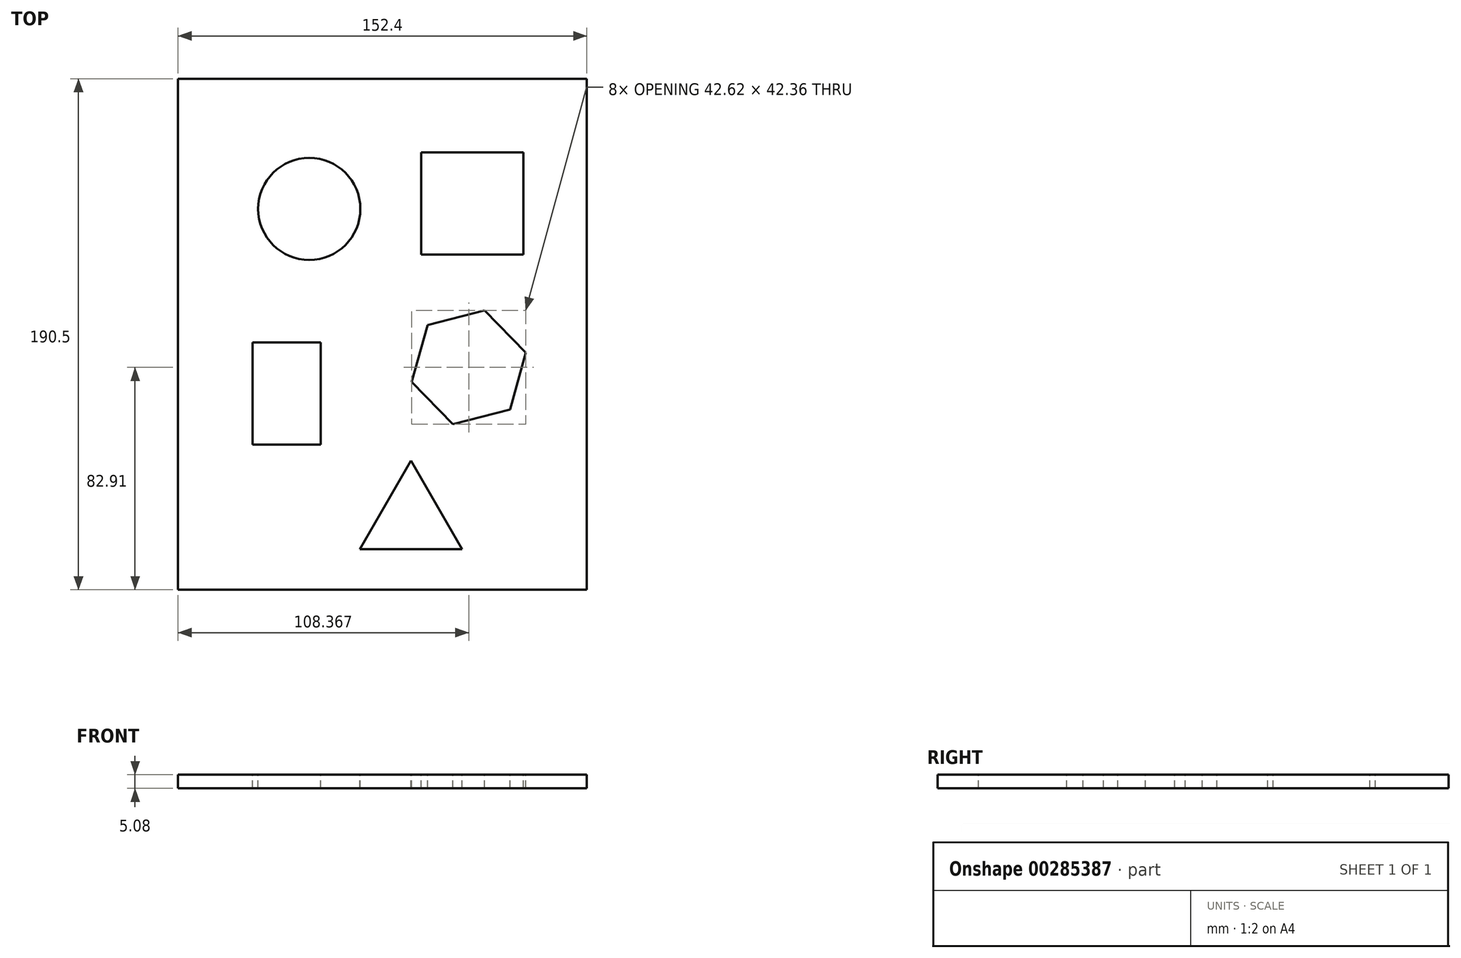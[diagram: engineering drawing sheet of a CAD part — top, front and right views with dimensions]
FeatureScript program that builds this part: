
annotation { "Feature Type Name" : "Feature", "Feature Type Description" : "" }
export const myFeature = defineFeature(function(context is Context, id is Id, definition is map)
    precondition{}
    {
        {
            var Q0;
            Q0=qCreatedBy(makeId("Top.planeOp"),FACE);
            var sketch = newSketch(context, id + "F0", { "sketchPlane" : qUnion([Q0])});
            skLineSegment(sketch, "E0.bottom", {"start": v(-86.56, 107.59) * mm, "end": v(65.84, 107.59) * mm});
            skLineSegment(sketch, "E0.top", {"start": v(-86.56, -82.91) * mm, "end": v(65.84, -82.91) * mm});
            skLineSegment(sketch, "E0.left", {"start": v(-86.56, 107.59) * mm, "end": v(-86.56, -82.91) * mm});
            skLineSegment(sketch, "E0.right", {"start": v(65.84, 107.59) * mm, "end": v(65.84, -82.91) * mm});
            skSolve(sketch);
        }
        {
            var Q0;
            Q0=makeQuery(id+"F0.imprint","IMPRINT",FACE,{"disambiguationData":[TD([[makeQuery(id+"F0.imprint","IMPRINT",EDGE,{"derivedFrom":sQuery(id+"F0.wireOp",EDGE,"E0.bottom")}),-1.0]])]});
            extrude(context, id + "F1", {"entities" : qUnion([Q0]), "depth" : 5.08 * mm});
        }
        {
            var Q0;
            Q0=makeQuery(id+"F1.opExtrude","CAP_FACE",FACE,{"disambiguationData":[OSD([sQuery(id+"F0.wireOp",EDGE,"E0.bottom"),sQuery(id+"F0.wireOp",EDGE,"E0.top"),sQuery(id+"F0.wireOp",EDGE,"E0.left"),sQuery(id+"F0.wireOp",EDGE,"E0.right")])],"isStart":false});
            var sketch = newSketch(context, id + "F2", { "sketchPlane" : qUnion([Q0])});
            skCircle(sketch, "E1", {"center": v(-37.64, 59.09) * mm, "radius": 19.05 * mm});
            skLineSegment(sketch, "E2.bottom", {"start": v(4.04, 80.2) * mm, "end": v(42.14, 80.2) * mm});
            skLineSegment(sketch, "E2.top", {"start": v(4.04, 42.1) * mm, "end": v(42.14, 42.1) * mm});
            skLineSegment(sketch, "E2.left", {"start": v(4.04, 80.2) * mm, "end": v(4.04, 42.1) * mm});
            skLineSegment(sketch, "E2.right", {"start": v(42.14, 80.2) * mm, "end": v(42.14, 42.1) * mm});
            skLineSegment(sketch, "E3.bottom", {"start": v(-58.8, 9.34) * mm, "end": v(-33.4, 9.34) * mm});
            skLineSegment(sketch, "E3.top", {"start": v(-58.8, -28.76) * mm, "end": v(-33.4, -28.76) * mm});
            skLineSegment(sketch, "E3.left", {"start": v(-58.8, 9.34) * mm, "end": v(-58.8, -28.76) * mm});
            skLineSegment(sketch, "E3.right", {"start": v(-33.4, 9.34) * mm, "end": v(-33.4, -28.76) * mm});
            skCircle(sketch, "E4.cCircle", {"center": v(21.8, 0) * mm, "radius": 19.05 * mm, "construction": true});
            skLineSegment(sketch, "E4.0", {"start": v(37.18, -15.73) * mm, "end": v(15.87, -21.18) * mm});
            skLineSegment(sketch, "E4.1", {"start": v(15.87, -21.18) * mm, "end": v(0.5, -5.45) * mm});
            skLineSegment(sketch, "E4.2", {"start": v(0.5, -5.45) * mm, "end": v(6.43, 15.73) * mm});
            skLineSegment(sketch, "E4.3", {"start": v(6.43, 15.73) * mm, "end": v(27.74, 21.18) * mm});
            skLineSegment(sketch, "E4.4", {"start": v(27.74, 21.18) * mm, "end": v(43.12, 5.45) * mm});
            skLineSegment(sketch, "E4.5", {"start": v(43.12, 5.45) * mm, "end": v(37.18, -15.73) * mm});
            skPoint(sketch, "E4.0.midPoint", {"position": v(26.52, -18.46) * mm});
            skLineSegment(sketch, "E5", {"start": v(0.3, -34.78) * mm, "end": v(-18.75, -67.77) * mm});
            skLineSegment(sketch, "E6", {"start": v(-18.75, -67.77) * mm, "end": v(19.35, -67.77) * mm});
            skLineSegment(sketch, "E7", {"start": v(19.35, -67.77) * mm, "end": v(0.3, -34.78) * mm});
            skSolve(sketch);
        }
        {
            var Q0;
            Q0=makeQuery(id+"F2.imprint","IMPRINT",FACE,{"disambiguationData":[TD([[makeQuery(id+"F2.imprint","IMPRINT",EDGE,{"derivedFrom":sQuery(id+"F2.wireOp",EDGE,"E2.bottom")}),-1.0]])]});
            var Q1;
            Q1=makeQuery(id+"F2.imprint","IMPRINT",FACE,{"disambiguationData":[TD([[makeQuery(id+"F2.imprint","IMPRINT",EDGE,{"derivedFrom":sQuery(id+"F2.wireOp",EDGE,"E5")}),1.0]])]});
            var Q2;
            Q2=makeQuery(id+"F2.imprint","IMPRINT",FACE,{"disambiguationData":[TD([[makeQuery(id+"F2.imprint","IMPRINT",EDGE,{"derivedFrom":sQuery(id+"F2.wireOp",EDGE,"E1")}),1.0]])]});
            var Q3;
            Q3=makeQuery(id+"F2.imprint","IMPRINT",FACE,{"disambiguationData":[TD([[makeQuery(id+"F2.imprint","IMPRINT",EDGE,{"derivedFrom":sQuery(id+"F2.wireOp",EDGE,"E4.0")}),-1.0]])]});
            var Q4;
            Q4=makeQuery(id+"F2.imprint","IMPRINT",FACE,{"disambiguationData":[TD([[makeQuery(id+"F2.imprint","IMPRINT",EDGE,{"derivedFrom":sQuery(id+"F2.wireOp",EDGE,"E3.bottom")}),-1.0]])]});
            extrude(context, id + "F3", {"entities" : qUnion([Q0, Q1, Q2, Q3, Q4]), "operationType" : NewBodyOperationType.REMOVE, "oppositeDirection" : true, "depth" : 25.4 * mm});
        }
    });
